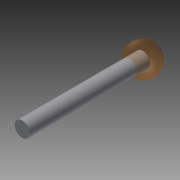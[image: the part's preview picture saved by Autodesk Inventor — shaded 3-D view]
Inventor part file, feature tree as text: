
AUTODESK INVENTOR PART (.ipt)
format: ipt  version: 2015 SP1 (Build 190203100, 203)  size: 103,936 bytes
history: native  units: in
note: dims shown in document units (in); Inventor stores cm internally (conversion verified against a paired STEP export)
features: sketch x2, extrude x1, other x1, revolve x1
ambient origin geometry x8: Origin, YZ Plane, XZ Plane, XY Plane, X Axis, Y Axis, Z Axis, Center Point
bodies: Solid1 (feature_tree)
feature tree (5):
  extrude  "Extrusion1"  Depth=0.5in
  sketch  "Sketch1"  dims[d1=90.0deg d2=0.5in]
  other  "Srf1"
  sketch  "Sketch2"  dims[d3=2.5in d4=0.0in]
  revolve  "RevolutionSrf1"  [1 undecoded]
note: 1 required parameter value undecoded (feature->parameter linkage not recoverable at this tier; creation-order binding heuristic only, values carry confidence <= 0.55)
